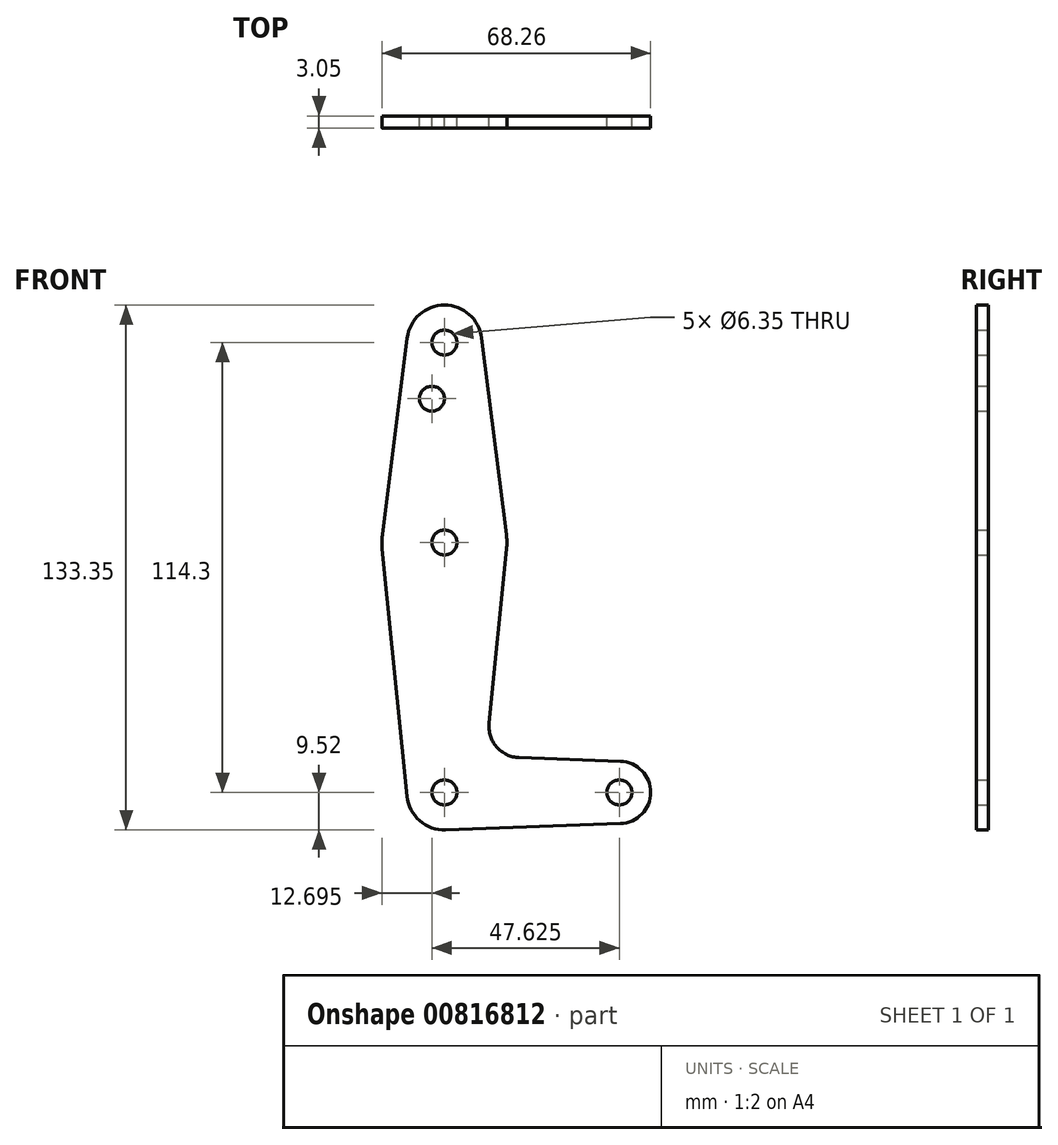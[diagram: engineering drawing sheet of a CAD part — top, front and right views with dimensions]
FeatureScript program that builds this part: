
annotation { "Feature Type Name" : "Feature", "Feature Type Description" : "" }
export const myFeature = defineFeature(function(context is Context, id is Id, definition is map)
    precondition{}
    {
        {
            var Q0;
            Q0=qCreatedBy(makeId("Front.planeOp"),FACE);
            var sketch = newSketch(context, id + "F0", { "sketchPlane" : qUnion([Q0])});
            skLineSegment(sketch, "E0", {"start": v(0, 0) * mm, "end": v(0, 114.3) * mm, "construction": true});
            skLineSegment(sketch, "E1", {"start": v(0, 0) * mm, "end": v(44.45, 0) * mm, "construction": true});
            skCircle(sketch, "E2", {"center": v(0, 114.3) * mm, "radius": 9.53 * mm});
            skCircle(sketch, "E3", {"center": v(0, 63.5) * mm, "radius": 15.88 * mm});
            skCircle(sketch, "E4", {"center": v(0, 0) * mm, "radius": 9.53 * mm});
            skCircle(sketch, "E5", {"center": v(44.45, 0) * mm, "radius": 7.94 * mm});
            skLineSegment(sketch, "E6", {"start": v(-9.45, 115.5) * mm, "end": v(-15.75, 65.48) * mm});
            skLineSegment(sketch, "E7", {"start": v(9.45, 115.5) * mm, "end": v(15.75, 65.48) * mm});
            skLineSegment(sketch, "E8", {"start": v(15.8, 61.91) * mm, "end": v(11.34, 17.6) * mm});
            skLineSegment(sketch, "E9", {"start": v(-9.48, -0.95) * mm, "end": v(-15.8, 61.91) * mm});
            skLineSegment(sketch, "E10", {"start": v(44.73, 7.93) * mm, "end": v(18.97, 8.85) * mm});
            skLineSegment(sketch, "E11", {"start": v(0.34, -9.52) * mm, "end": v(44.73, -7.93) * mm});
            skCircle(sketch, "E12", {"center": v(0, 114.3) * mm, "radius": 3.18 * mm});
            skCircle(sketch, "E13", {"center": v(0, 63.5) * mm, "radius": 3.18 * mm});
            skCircle(sketch, "E14", {"center": v(0, 0) * mm, "radius": 3.18 * mm});
            skCircle(sketch, "E15", {"center": v(44.45, 0) * mm, "radius": 3.18 * mm});
            skCircle(sketch, "E16", {"center": v(-3.18, 100.03) * mm, "radius": 3.18 * mm});
            skArc(sketch, "E17.filletArc", {"start": v(11.34, 17.6) * mm, "mid": v(13.26, 11.57) * mm, "end": v(18.97, 8.85) * mm});
            skSolve(sketch);
        }
        {
            var Q0;
            Q0 = qSketchRegion(id + "F0", true);
            extrude(context, id + "F1", {"entities" : qUnion([Q0]), "depth" : 3.05 * mm, "offsetDistance" : 25.4 * mm});
        }
    });
